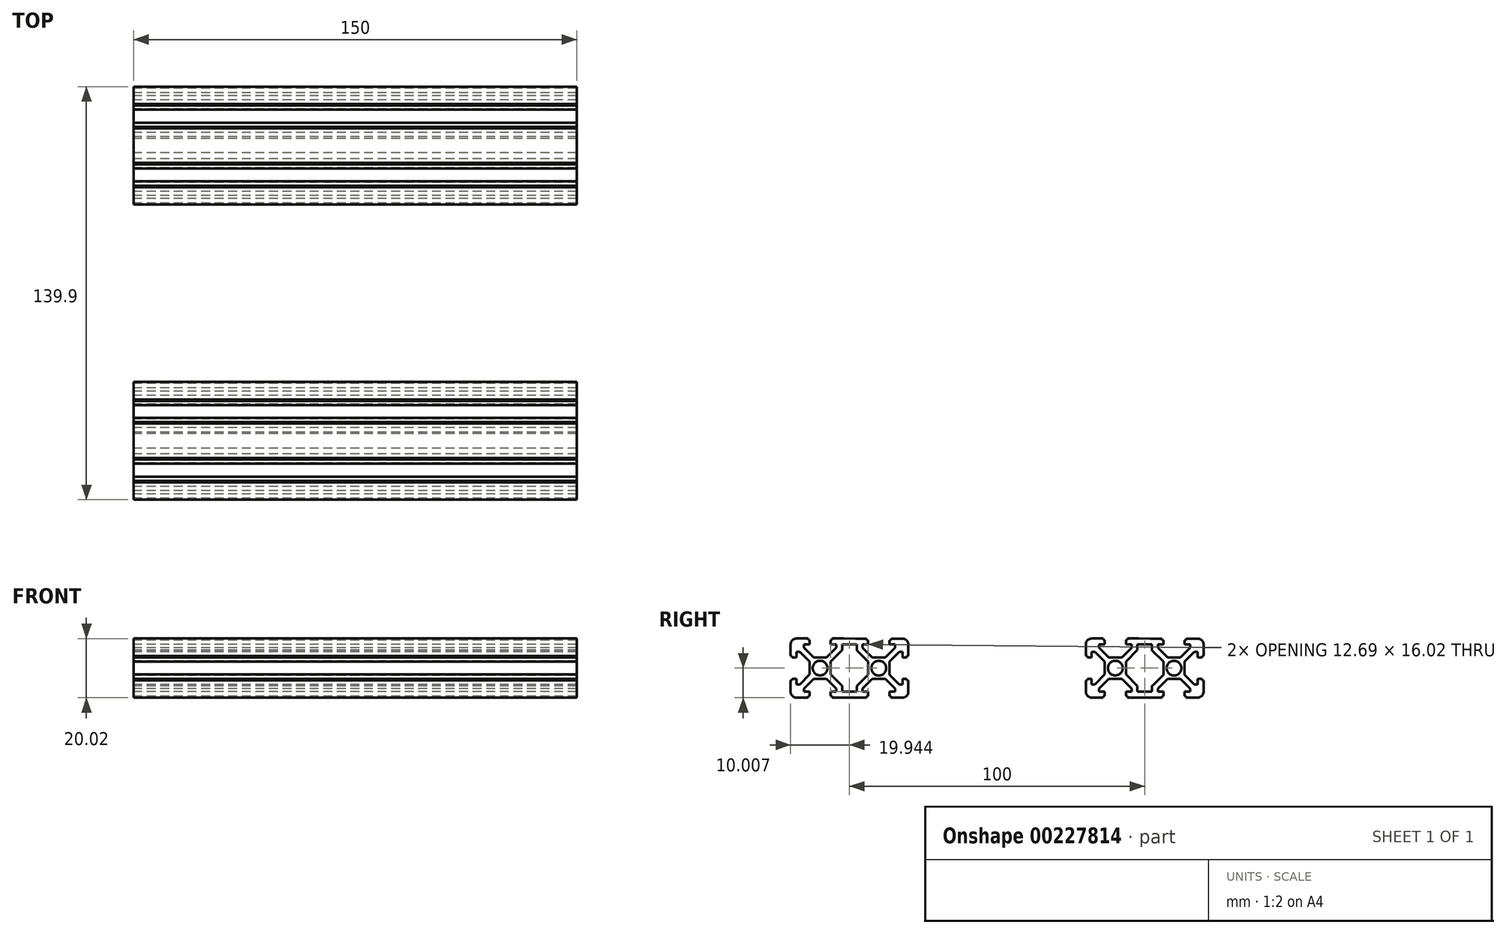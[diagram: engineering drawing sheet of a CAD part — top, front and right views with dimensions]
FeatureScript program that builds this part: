
annotation { "Feature Type Name" : "Feature", "Feature Type Description" : "" }
export const myFeature = defineFeature(function(context is Context, id is Id, definition is map)
    precondition{}
    {
        {
            var Q0;
            Q0=qCreatedBy(makeId("Right.planeOp"),FACE);
            var sketch = newSketch(context, id + "F0", { "sketchPlane" : qUnion([Q0])});
            skLineSegment(sketch, "E0", {"start": v(7.66, 9.4) * mm, "end": v(3.75, 9.4) * mm});
            skLineSegment(sketch, "E1", {"start": v(-8.35, -10.6) * mm, "end": v(-4.45, -10.6) * mm});
            skLineSegment(sketch, "E2", {"start": v(9.65, -8.6) * mm, "end": v(9.65, -4.7) * mm});
            skLineSegment(sketch, "E3", {"start": v(9.65, 9.4) * mm, "end": v(9.65, 9.37) * mm});
            skCircle(sketch, "E4", {"center": v(-0.35, -0.6) * mm, "radius": 2.5 * mm});
            skLineSegment(sketch, "E5", {"start": v(-3.95, -0.6) * mm, "end": v(-3.95, 1.6) * mm});
            skLineSegment(sketch, "E6", {"start": v(-0.35, 3) * mm, "end": v(-2.54, 3) * mm});
            skLineSegment(sketch, "E7", {"start": v(3.25, -0.6) * mm, "end": v(3.25, 1.6) * mm});
            skLineSegment(sketch, "E8", {"start": v(3.25, 8.9) * mm, "end": v(3.25, 7.4) * mm});
            skLineSegment(sketch, "E9", {"start": v(-0.35, -4.2) * mm, "end": v(1.83, -4.2) * mm});
            skLineSegment(sketch, "E10", {"start": v(9.15, -4.2) * mm, "end": v(7.65, -4.2) * mm});
            skLineSegment(sketch, "E11", {"start": v(-3.95, -0.6) * mm, "end": v(-3.95, -2.78) * mm});
            skLineSegment(sketch, "E12.0", {"start": v(-7.27, 4.9) * mm, "end": v(-3.95, 1.6) * mm});
            skLineSegment(sketch, "E13.0", {"start": v(9.67, 9.39) * mm, "end": v(9.65, 9.37) * mm});
            skLineSegment(sketch, "E14.0", {"start": v(5.15, 6.32) * mm, "end": v(1.83, 3) * mm});
            skPoint(sketch, "E15.startSnap0", {"position": v(-0.35, 9.4) * mm});
            skLineSegment(sketch, "E16", {"start": v(5.15, 7.4) * mm, "end": v(5.15, 6.32) * mm});
            skLineSegment(sketch, "E17", {"start": v(7.65, -6.1) * mm, "end": v(6.56, -6.1) * mm});
            skLineSegment(sketch, "E18", {"start": v(7.65, 4.9) * mm, "end": v(6.56, 4.9) * mm});
            skLineSegment(sketch, "E19", {"start": v(-5.85, 7.4) * mm, "end": v(-5.85, 6.32) * mm});
            skLineSegment(sketch, "E20.trimOffspring", {"start": v(-4.45, 9.4) * mm, "end": v(-8.35, 9.4) * mm});
            skLineSegment(sketch, "E21.trimOffspring", {"start": v(-3.95, 7.4) * mm, "end": v(-5.85, 7.4) * mm});
            skLineSegment(sketch, "E22.trimOffspring", {"start": v(3.25, 7.4) * mm, "end": v(3.25, 8.9) * mm});
            skLineSegment(sketch, "E23.trimOffspring", {"start": v(-3.95, 7.4) * mm, "end": v(-3.95, 8.9) * mm});
            skPoint(sketch, "E15.start.orphan", {"position": v(-0.35, 12.95) * mm});
            skLineSegment(sketch, "E24.trimOffspring", {"start": v(-2.54, 3) * mm, "end": v(1.83, 3) * mm});
            skLineSegment(sketch, "E25.trimOffspring", {"start": v(3.75, -10.6) * mm, "end": v(7.65, -10.6) * mm});
            skLineSegment(sketch, "E26.trimOffspring", {"start": v(3.25, -8.6) * mm, "end": v(5.15, -8.6) * mm});
            skLineSegment(sketch, "E27.trimOffspring", {"start": v(-3.95, -8.6) * mm, "end": v(-3.95, -10.1) * mm});
            skLineSegment(sketch, "E28.trimOffspring", {"start": v(3.25, -8.6) * mm, "end": v(3.25, -10.1) * mm});
            skLineSegment(sketch, "E29.trimOffspring", {"start": v(7.65, 3) * mm, "end": v(9.15, 3) * mm});
            skLineSegment(sketch, "E30.trimOffspring", {"start": v(1.83, -4.2) * mm, "end": v(-2.54, -4.2) * mm});
            skLineSegment(sketch, "E31.trimOffspring", {"start": v(7.65, -4.2) * mm, "end": v(9.15, -4.2) * mm});
            skLineSegment(sketch, "E32.trimOffspring", {"start": v(6.56, 4.9) * mm, "end": v(3.25, 1.6) * mm});
            skLineSegment(sketch, "E33.trimOffspring", {"start": v(5.15, 7.4) * mm, "end": v(3.25, 7.4) * mm});
            skLineSegment(sketch, "E34.trimOffspring", {"start": v(7.65, 4.9) * mm, "end": v(7.65, 3) * mm});
            skLineSegment(sketch, "E35.trimOffspring", {"start": v(9.65, 4.9) * mm, "end": v(9.65, 3.5) * mm});
            skLineSegment(sketch, "E36", {"start": v(9.66, 7.4) * mm, "end": v(9.65, 4.9) * mm});
            skLineSegment(sketch, "E37.trimOffspring", {"start": v(3.25, 1.6) * mm, "end": v(3.25, -2.78) * mm});
            skLineSegment(sketch, "E38.trimOffspring", {"start": v(3.25, -2.78) * mm, "end": v(6.56, -6.1) * mm});
            skLineSegment(sketch, "E39.trimOffspring", {"start": v(-2.54, -4.2) * mm, "end": v(-5.85, -7.5) * mm});
            skLineSegment(sketch, "E40.trimOffspring", {"start": v(1.83, -4.2) * mm, "end": v(5.15, -7.5) * mm});
            skLineSegment(sketch, "E41.trimOffspring", {"start": v(-3.95, -2.78) * mm, "end": v(-7.27, -6.1) * mm});
            skLineSegment(sketch, "E42.trimOffspring", {"start": v(-0.26, -0.6) * mm, "end": v(-0.24, -0.61) * mm});
            skLineSegment(sketch, "E43.trimOffspring", {"start": v(-5.85, 6.32) * mm, "end": v(-2.54, 3) * mm});
            skLineSegment(sketch, "E44.trimOffspring", {"start": v(-5.85, -7.5) * mm, "end": v(-5.85, -8.6) * mm});
            skLineSegment(sketch, "E45.trimOffspring", {"start": v(-5.85, -8.6) * mm, "end": v(-3.95, -8.6) * mm});
            skLineSegment(sketch, "E46.trimOffspring", {"start": v(5.15, -7.5) * mm, "end": v(5.15, -8.6) * mm});
            skLineSegment(sketch, "E47.trimOffspring", {"start": v(7.65, -6.1) * mm, "end": v(7.65, -4.2) * mm});
            skPoint(sketch, "E48.visualSharp", {"position": v(-10.35, 9.4) * mm});
            skPoint(sketch, "E49.newPointA", {"position": v(9.65, 9.4) * mm});
            skArc(sketch, "E49.filletArc", {"start": v(9.66, 7.4) * mm, "mid": v(9.07, 8.82) * mm, "end": v(7.66, 9.4) * mm});
            skPoint(sketch, "E50.visualSharp", {"position": v(9.65, -10.6) * mm});
            skArc(sketch, "E50.filletArc", {"start": v(7.65, -10.6) * mm, "mid": v(9.06, -10) * mm, "end": v(9.65, -8.6) * mm});
            skPoint(sketch, "E51.visualSharp", {"position": v(-10.35, -10.6) * mm});
            skLineSegment(sketch, "E52", {"start": v(-3.95, -10.1) * mm, "end": v(-4.45, -10.1) * mm});
            skLineSegment(sketch, "E53", {"start": v(-4.45, -10.1) * mm, "end": v(-4.45, -10.6) * mm});
            skLineSegment(sketch, "E54", {"start": v(3.75, -10.6) * mm, "end": v(3.75, -10.1) * mm});
            skLineSegment(sketch, "E55", {"start": v(3.75, -10.1) * mm, "end": v(3.25, -10.1) * mm});
            skLineSegment(sketch, "E56", {"start": v(9.15, -4.2) * mm, "end": v(9.15, -4.7) * mm});
            skLineSegment(sketch, "E57", {"start": v(9.15, -4.7) * mm, "end": v(9.65, -4.7) * mm});
            skLineSegment(sketch, "E58", {"start": v(9.15, 3) * mm, "end": v(9.15, 3.5) * mm});
            skLineSegment(sketch, "E59", {"start": v(9.15, 3.5) * mm, "end": v(9.65, 3.5) * mm});
            skPoint(sketch, "E60.orphan", {"position": v(-10.35, -4.2) * mm});
            skPoint(sketch, "E61.start.orphan", {"position": v(9.65, 3) * mm});
            skPoint(sketch, "E62.start.orphan", {"position": v(3.25, -10.6) * mm});
            skPoint(sketch, "E63.orphan", {"position": v(-3.95, -10.6) * mm});
            skLineSegment(sketch, "E64", {"start": v(-3.95, 8.9) * mm, "end": v(-4.45, 8.9) * mm});
            skLineSegment(sketch, "E65", {"start": v(-4.45, 8.9) * mm, "end": v(-4.45, 9.4) * mm});
            skLineSegment(sketch, "E66", {"start": v(3.25, 8.9) * mm, "end": v(3.75, 8.9) * mm});
            skLineSegment(sketch, "E67", {"start": v(3.75, 8.9) * mm, "end": v(3.75, 9.4) * mm});
            skPoint(sketch, "E68.start.orphan", {"position": v(3.25, 9.4) * mm});
            skPoint(sketch, "E69.start.orphan", {"position": v(-3.95, 9.4) * mm});
            skLineSegment(sketch, "E70", {"start": v(-12.23, 9.43) * mm, "end": v(-16.14, 9.43) * mm});
            skLineSegment(sketch, "E71", {"start": v(-30.24, 7.43) * mm, "end": v(-30.24, 3.53) * mm});
            skLineSegment(sketch, "E72", {"start": v(-28.24, -10.57) * mm, "end": v(-24.34, -10.57) * mm});
            skLineSegment(sketch, "E73", {"start": v(-10.24, -4.7) * mm, "end": v(-10.24, -4.67) * mm});
            skLineSegment(sketch, "E74", {"start": v(-10.24, 9.43) * mm, "end": v(-10.24, 9.4) * mm});
            skCircle(sketch, "E75", {"center": v(-20.24, -0.57) * mm, "radius": 2.5 * mm});
            skLineSegment(sketch, "E76", {"start": v(-23.84, 4.45) * mm, "end": v(-23.84, 4.5) * mm});
            skLineSegment(sketch, "E77", {"start": v(-29.74, 3.03) * mm, "end": v(-28.24, 3.03) * mm});
            skLineSegment(sketch, "E78", {"start": v(-16.64, 4.45) * mm, "end": v(-16.64, 4.5) * mm});
            skLineSegment(sketch, "E79", {"start": v(-16.64, 8.93) * mm, "end": v(-16.64, 7.43) * mm});
            skLineSegment(sketch, "E80", {"start": v(-22.42, -4.17) * mm, "end": v(-18.05, -4.17) * mm});
            skLineSegment(sketch, "E81", {"start": v(-23.84, 4.5) * mm, "end": v(-23.84, 4.45) * mm});
            skLineSegment(sketch, "E82.0", {"start": v(-27.15, 4.93) * mm, "end": v(-23.84, 1.62) * mm});
            skLineSegment(sketch, "E83.0", {"start": v(-14.74, 6.35) * mm, "end": v(-18.05, 3.03) * mm});
            skPoint(sketch, "E84.startSnap0", {"position": v(-20.24, 9.43) * mm});
            skLineSegment(sketch, "E85", {"start": v(-14.74, 7.43) * mm, "end": v(-14.74, 6.35) * mm});
            skLineSegment(sketch, "E86", {"start": v(-25.74, 7.43) * mm, "end": v(-25.74, 6.35) * mm});
            skLineSegment(sketch, "E87.trimOffspring", {"start": v(-24.34, 9.43) * mm, "end": v(-28.24, 9.43) * mm});
            skLineSegment(sketch, "E88.trimOffspring", {"start": v(-23.84, 7.43) * mm, "end": v(-25.74, 7.43) * mm});
            skLineSegment(sketch, "E89.trimOffspring", {"start": v(-16.64, 7.43) * mm, "end": v(-16.64, 8.93) * mm});
            skLineSegment(sketch, "E90.trimOffspring", {"start": v(-23.84, 7.43) * mm, "end": v(-23.84, 8.93) * mm});
            skPoint(sketch, "E84.start.orphan", {"position": v(-20.24, 12.98) * mm});
            skLineSegment(sketch, "E91.trimOffspring", {"start": v(-30.24, -4.67) * mm, "end": v(-30.24, -8.57) * mm});
            skLineSegment(sketch, "E92.trimOffspring", {"start": v(-28.24, -4.17) * mm, "end": v(-28.24, -6.07) * mm});
            skLineSegment(sketch, "E93.trimOffspring", {"start": v(-22.42, 3.03) * mm, "end": v(-18.05, 3.03) * mm});
            skLineSegment(sketch, "E94.trimOffspring", {"start": v(-28.24, 3.03) * mm, "end": v(-29.74, 3.03) * mm});
            skLineSegment(sketch, "E95.trimOffspring", {"start": v(-28.24, -4.17) * mm, "end": v(-29.74, -4.17) * mm});
            skLineSegment(sketch, "E96.trimOffspring", {"start": v(-16.14, -10.57) * mm, "end": v(-12.24, -10.57) * mm});
            skLineSegment(sketch, "E97.trimOffspring", {"start": v(-16.64, -8.57) * mm, "end": v(-14.74, -8.57) * mm});
            skLineSegment(sketch, "E98.trimOffspring", {"start": v(-23.84, -8.57) * mm, "end": v(-23.84, -10.07) * mm});
            skLineSegment(sketch, "E99.trimOffspring", {"start": v(-16.64, -8.57) * mm, "end": v(-16.64, -10.07) * mm});
            skLineSegment(sketch, "E100.trimOffspring", {"start": v(-18.05, -4.17) * mm, "end": v(-22.42, -4.17) * mm});
            skLineSegment(sketch, "E101.trimOffspring", {"start": v(-13.32, 4.93) * mm, "end": v(-16.64, 1.62) * mm});
            skLineSegment(sketch, "E102.trimOffspring", {"start": v(-14.74, 7.43) * mm, "end": v(-16.64, 7.43) * mm});
            skLineSegment(sketch, "E103.trimOffspring", {"start": v(-16.64, 1.62) * mm, "end": v(-16.64, -2.75) * mm});
            skLineSegment(sketch, "E104.trimOffspring", {"start": v(-16.64, -2.75) * mm, "end": v(-13.32, -6.07) * mm});
            skLineSegment(sketch, "E105.trimOffspring", {"start": v(-22.42, -4.17) * mm, "end": v(-25.74, -7.48) * mm});
            skLineSegment(sketch, "E106.trimOffspring", {"start": v(-18.05, -4.17) * mm, "end": v(-14.74, -7.48) * mm});
            skLineSegment(sketch, "E107.trimOffspring", {"start": v(-23.84, -2.75) * mm, "end": v(-27.15, -6.07) * mm});
            skLineSegment(sketch, "E108.trimOffspring", {"start": v(-20.24, -0.57) * mm, "end": v(-20.22, -0.59) * mm});
            skLineSegment(sketch, "E109.trimOffspring", {"start": v(-28.24, 4.93) * mm, "end": v(-28.24, 3.03) * mm});
            skLineSegment(sketch, "E110.trimOffspring", {"start": v(-25.74, 6.35) * mm, "end": v(-22.42, 3.03) * mm});
            skLineSegment(sketch, "E111.trimOffspring", {"start": v(-27.15, 4.93) * mm, "end": v(-28.24, 4.93) * mm});
            skLineSegment(sketch, "E112.trimOffspring", {"start": v(-27.15, -6.07) * mm, "end": v(-28.24, -6.07) * mm});
            skLineSegment(sketch, "E113.trimOffspring", {"start": v(-25.74, -7.48) * mm, "end": v(-25.74, -8.57) * mm});
            skLineSegment(sketch, "E114.trimOffspring", {"start": v(-29, -9.37) * mm, "end": v(-30.2, -10.57) * mm});
            skLineSegment(sketch, "E115.trimOffspring", {"start": v(-25.74, -8.57) * mm, "end": v(-23.84, -8.57) * mm});
            skLineSegment(sketch, "E116.trimOffspring", {"start": v(-14.74, -7.48) * mm, "end": v(-14.74, -8.57) * mm});
            skPoint(sketch, "E117.visualSharp", {"position": v(-30.24, 9.43) * mm});
            skArc(sketch, "E117.filletArc", {"start": v(-28.24, 9.43) * mm, "mid": v(-29.65, 8.85) * mm, "end": v(-30.24, 7.43) * mm});
            skPoint(sketch, "E118.newPointA", {"position": v(-10.24, 9.43) * mm});
            skPoint(sketch, "E119.visualSharp", {"position": v(-10.24, -10.57) * mm});
            skPoint(sketch, "E120.visualSharp", {"position": v(-30.24, -10.57) * mm});
            skArc(sketch, "E120.filletArc", {"start": v(-30.24, -8.57) * mm, "mid": v(-29.65, -9.98) * mm, "end": v(-28.24, -10.57) * mm});
            skLineSegment(sketch, "E121", {"start": v(-29.74, 3.03) * mm, "end": v(-29.74, 3.53) * mm});
            skLineSegment(sketch, "E122", {"start": v(-29.74, 3.53) * mm, "end": v(-30.24, 3.53) * mm});
            skLineSegment(sketch, "E123", {"start": v(-29.74, -4.17) * mm, "end": v(-29.74, -4.67) * mm});
            skLineSegment(sketch, "E124", {"start": v(-29.74, -4.67) * mm, "end": v(-30.24, -4.67) * mm});
            skLineSegment(sketch, "E125", {"start": v(-23.84, -10.07) * mm, "end": v(-24.34, -10.07) * mm});
            skLineSegment(sketch, "E126", {"start": v(-24.34, -10.07) * mm, "end": v(-24.34, -10.57) * mm});
            skLineSegment(sketch, "E127", {"start": v(-16.14, -10.57) * mm, "end": v(-16.14, -10.07) * mm});
            skLineSegment(sketch, "E128", {"start": v(-16.14, -10.07) * mm, "end": v(-16.64, -10.07) * mm});
            skPoint(sketch, "E129.orphan", {"position": v(-30.24, -4.17) * mm});
            skPoint(sketch, "E130.start.orphan", {"position": v(-10.24, 3.03) * mm});
            skPoint(sketch, "E131.start.orphan", {"position": v(-16.64, -10.57) * mm});
            skPoint(sketch, "E132.orphan", {"position": v(-23.84, -10.57) * mm});
            skLineSegment(sketch, "E133", {"start": v(-23.84, 8.93) * mm, "end": v(-24.34, 8.93) * mm});
            skLineSegment(sketch, "E134", {"start": v(-24.34, 8.93) * mm, "end": v(-24.34, 9.43) * mm});
            skLineSegment(sketch, "E135", {"start": v(-16.64, 8.93) * mm, "end": v(-16.14, 8.93) * mm});
            skLineSegment(sketch, "E136", {"start": v(-16.14, 8.93) * mm, "end": v(-16.14, 9.43) * mm});
            skPoint(sketch, "E137.start.orphan", {"position": v(-16.64, 9.43) * mm});
            skPoint(sketch, "E138.start.orphan", {"position": v(-23.84, 9.43) * mm});
            skPoint(sketch, "E139.end.orphan", {"position": v(-10.24, 3.53) * mm});
            skLineSegment(sketch, "E140", {"start": v(-12.23, 9.43) * mm, "end": v(-8.35, 9.4) * mm});
            skArc(sketch, "E141.trimOffspring", {"start": v(-12.2, 9.43) * mm, "mid": v(-12.22, 9.43) * mm, "end": v(-12.23, 9.43) * mm});
            skLineSegment(sketch, "E142.trimOffspring", {"start": v(-23.84, 1.62) * mm, "end": v(-23.84, -2.75) * mm});
            skLineSegment(sketch, "E143", {"start": v(-12.24, -10.57) * mm, "end": v(-8.38, -10.6) * mm});
            skLineSegment(sketch, "E144", {"start": v(-8.38, -10.6) * mm, "end": v(-8.35, -10.6) * mm});
            skLineSegment(sketch, "E145.0", {"start": v(-12.74, 5.52) * mm, "end": v(-16.64, 1.62) * mm});
            skLineSegment(sketch, "E145.1", {"start": v(-12.74, 7.43) * mm, "end": v(-12.74, 5.52) * mm});
            skLineSegment(sketch, "E145.2", {"start": v(-12.74, 9.43) * mm, "end": v(-16.64, 9.43) * mm});
            skLineSegment(sketch, "E146.0", {"start": v(-7.85, 7.4) * mm, "end": v(-7.85, 6.32) * mm});
            skLineSegment(sketch, "E147", {"start": v(-7.27, 4.9) * mm, "end": v(-7.85, 5.5) * mm});
            skLineSegment(sketch, "E148", {"start": v(-7.85, 6.32) * mm, "end": v(-7.85, 5.5) * mm});
            skLineSegment(sketch, "E149", {"start": v(-12.74, 7.43) * mm, "end": v(-7.85, 7.4) * mm});
            skLineSegment(sketch, "E150.0", {"start": v(-12.74, -7.48) * mm, "end": v(-12.74, -8.57) * mm});
            skLineSegment(sketch, "E151.0", {"start": v(-7.85, -7.5) * mm, "end": v(-7.85, -8.6) * mm});
            skLineSegment(sketch, "E152", {"start": v(-13.32, -6.07) * mm, "end": v(-12.74, -6.65) * mm});
            skLineSegment(sketch, "E153", {"start": v(-7.27, -6.1) * mm, "end": v(-7.85, -6.7) * mm});
            skLineSegment(sketch, "E154", {"start": v(-12.74, -7.48) * mm, "end": v(-12.74, -6.65) * mm});
            skLineSegment(sketch, "E155", {"start": v(-7.85, -7.5) * mm, "end": v(-7.85, -6.7) * mm});
            skPoint(sketch, "E156.end.orphan", {"position": v(-10.35, -4.7) * mm});
            skLineSegment(sketch, "E157", {"start": v(-12.74, -8.57) * mm, "end": v(-7.85, -8.6) * mm});
            skSolve(sketch);
        }
        {
            var Q0;
            Q0=makeQuery(id+"F0.imprint","IMPRINT",FACE,{"disambiguationData":[TD([[makeQuery(id+"F0.imprint","IMPRINT",EDGE,{"derivedFrom":sQuery(id+"F0.wireOp",EDGE,"E0")}),1.0]])]});
            extrude(context, id + "F1", {"entities" : qUnion([Q0]), "depth" : 150 * mm});
        }
        {
            var Q0;
            Q0=makeQuery(id+"F1.opExtrude","SWEPT_BODY",BODY,{"disambiguationData":[OSD([sQuery(id+"F0.wireOp",EDGE,"E0"),sQuery(id+"F0.wireOp",EDGE,"E1"),sQuery(id+"F0.wireOp",EDGE,"E2"),sQuery(id+"F0.wireOp",EDGE,"E4"),sQuery(id+"F0.wireOp",EDGE,"E5"),sQuery(id+"F0.wireOp",EDGE,"E11"),sQuery(id+"F0.wireOp",EDGE,"E12.0"),sQuery(id+"F0.wireOp",EDGE,"E14.0"),sQuery(id+"F0.wireOp",EDGE,"E16"),sQuery(id+"F0.wireOp",EDGE,"E17"),sQuery(id+"F0.wireOp",EDGE,"E18"),sQuery(id+"F0.wireOp",EDGE,"E19"),sQuery(id+"F0.wireOp",EDGE,"E20.trimOffspring"),sQuery(id+"F0.wireOp",EDGE,"E21.trimOffspring"),sQuery(id+"F0.wireOp",EDGE,"E22.trimOffspring"),sQuery(id+"F0.wireOp",EDGE,"E23.trimOffspring"),sQuery(id+"F0.wireOp",EDGE,"E24.trimOffspring"),sQuery(id+"F0.wireOp",EDGE,"E25.trimOffspring"),sQuery(id+"F0.wireOp",EDGE,"E26.trimOffspring"),sQuery(id+"F0.wireOp",EDGE,"E27.trimOffspring"),sQuery(id+"F0.wireOp",EDGE,"E28.trimOffspring"),sQuery(id+"F0.wireOp",EDGE,"E29.trimOffspring"),sQuery(id+"F0.wireOp",EDGE,"E30.trimOffspring"),sQuery(id+"F0.wireOp",EDGE,"E31.trimOffspring"),sQuery(id+"F0.wireOp",EDGE,"E32.trimOffspring"),sQuery(id+"F0.wireOp",EDGE,"E33.trimOffspring"),sQuery(id+"F0.wireOp",EDGE,"E34.trimOffspring"),sQuery(id+"F0.wireOp",EDGE,"E35.trimOffspring"),sQuery(id+"F0.wireOp",EDGE,"E36"),sQuery(id+"F0.wireOp",EDGE,"E37.trimOffspring"),sQuery(id+"F0.wireOp",EDGE,"E38.trimOffspring"),sQuery(id+"F0.wireOp",EDGE,"E39.trimOffspring"),sQuery(id+"F0.wireOp",EDGE,"E40.trimOffspring"),sQuery(id+"F0.wireOp",EDGE,"E41.trimOffspring"),sQuery(id+"F0.wireOp",EDGE,"E43.trimOffspring"),sQuery(id+"F0.wireOp",EDGE,"E44.trimOffspring"),sQuery(id+"F0.wireOp",EDGE,"E45.trimOffspring"),sQuery(id+"F0.wireOp",EDGE,"E46.trimOffspring"),sQuery(id+"F0.wireOp",EDGE,"E47.trimOffspring"),sQuery(id+"F0.wireOp",EDGE,"E49.filletArc"),sQuery(id+"F0.wireOp",EDGE,"E50.filletArc"),sQuery(id+"F0.wireOp",EDGE,"E52"),sQuery(id+"F0.wireOp",EDGE,"E53"),sQuery(id+"F0.wireOp",EDGE,"E54"),sQuery(id+"F0.wireOp",EDGE,"E55"),sQuery(id+"F0.wireOp",EDGE,"E56"),sQuery(id+"F0.wireOp",EDGE,"E57"),sQuery(id+"F0.wireOp",EDGE,"E58"),sQuery(id+"F0.wireOp",EDGE,"E59"),sQuery(id+"F0.wireOp",EDGE,"E64"),sQuery(id+"F0.wireOp",EDGE,"E65"),sQuery(id+"F0.wireOp",EDGE,"E66"),sQuery(id+"F0.wireOp",EDGE,"E67"),sQuery(id+"F0.wireOp",EDGE,"E70"),sQuery(id+"F0.wireOp",EDGE,"E71"),sQuery(id+"F0.wireOp",EDGE,"E72"),sQuery(id+"F0.wireOp",EDGE,"E75"),sQuery(id+"F0.wireOp",EDGE,"E82.0"),sQuery(id+"F0.wireOp",EDGE,"E83.0"),sQuery(id+"F0.wireOp",EDGE,"E85"),sQuery(id+"F0.wireOp",EDGE,"E86"),sQuery(id+"F0.wireOp",EDGE,"E87.trimOffspring"),sQuery(id+"F0.wireOp",EDGE,"E88.trimOffspring"),sQuery(id+"F0.wireOp",EDGE,"E89.trimOffspring"),sQuery(id+"F0.wireOp",EDGE,"E90.trimOffspring"),sQuery(id+"F0.wireOp",EDGE,"E91.trimOffspring"),sQuery(id+"F0.wireOp",EDGE,"E92.trimOffspring"),sQuery(id+"F0.wireOp",EDGE,"E93.trimOffspring"),sQuery(id+"F0.wireOp",EDGE,"E94.trimOffspring"),sQuery(id+"F0.wireOp",EDGE,"E95.trimOffspring"),sQuery(id+"F0.wireOp",EDGE,"E96.trimOffspring"),sQuery(id+"F0.wireOp",EDGE,"E97.trimOffspring"),sQuery(id+"F0.wireOp",EDGE,"E98.trimOffspring"),sQuery(id+"F0.wireOp",EDGE,"E99.trimOffspring"),sQuery(id+"F0.wireOp",EDGE,"E100.trimOffspring"),sQuery(id+"F0.wireOp",EDGE,"E102.trimOffspring"),sQuery(id+"F0.wireOp",EDGE,"E103.trimOffspring"),sQuery(id+"F0.wireOp",EDGE,"E104.trimOffspring"),sQuery(id+"F0.wireOp",EDGE,"E105.trimOffspring"),sQuery(id+"F0.wireOp",EDGE,"E106.trimOffspring"),sQuery(id+"F0.wireOp",EDGE,"E107.trimOffspring"),sQuery(id+"F0.wireOp",EDGE,"E109.trimOffspring"),sQuery(id+"F0.wireOp",EDGE,"E110.trimOffspring"),sQuery(id+"F0.wireOp",EDGE,"E111.trimOffspring"),sQuery(id+"F0.wireOp",EDGE,"E112.trimOffspring"),sQuery(id+"F0.wireOp",EDGE,"E113.trimOffspring"),sQuery(id+"F0.wireOp",EDGE,"E115.trimOffspring"),sQuery(id+"F0.wireOp",EDGE,"E116.trimOffspring"),sQuery(id+"F0.wireOp",EDGE,"E117.filletArc"),sQuery(id+"F0.wireOp",EDGE,"E120.filletArc"),sQuery(id+"F0.wireOp",EDGE,"E121"),sQuery(id+"F0.wireOp",EDGE,"E122"),sQuery(id+"F0.wireOp",EDGE,"E123"),sQuery(id+"F0.wireOp",EDGE,"E124"),sQuery(id+"F0.wireOp",EDGE,"E125"),sQuery(id+"F0.wireOp",EDGE,"E126"),sQuery(id+"F0.wireOp",EDGE,"E127"),sQuery(id+"F0.wireOp",EDGE,"E128"),sQuery(id+"F0.wireOp",EDGE,"E133"),sQuery(id+"F0.wireOp",EDGE,"E134"),sQuery(id+"F0.wireOp",EDGE,"E135"),sQuery(id+"F0.wireOp",EDGE,"E136"),sQuery(id+"F0.wireOp",EDGE,"E140"),sQuery(id+"F0.wireOp",EDGE,"E142.trimOffspring"),sQuery(id+"F0.wireOp",EDGE,"E143"),sQuery(id+"F0.wireOp",EDGE,"E144"),sQuery(id+"F0.wireOp",EDGE,"E145.0"),sQuery(id+"F0.wireOp",EDGE,"E145.1"),sQuery(id+"F0.wireOp",EDGE,"E145.2"),sQuery(id+"F0.wireOp",EDGE,"E146.0"),sQuery(id+"F0.wireOp",EDGE,"E147"),sQuery(id+"F0.wireOp",EDGE,"E148"),sQuery(id+"F0.wireOp",EDGE,"E149"),sQuery(id+"F0.wireOp",EDGE,"E150.0"),sQuery(id+"F0.wireOp",EDGE,"E151.0"),sQuery(id+"F0.wireOp",EDGE,"E152"),sQuery(id+"F0.wireOp",EDGE,"E153"),sQuery(id+"F0.wireOp",EDGE,"E154"),sQuery(id+"F0.wireOp",EDGE,"E155"),sQuery(id+"F0.wireOp",EDGE,"E157")])]});
            var Q1;
            Q1=makeQuery(id+"F1.opExtrude","CAP_EDGE",EDGE,{"disambiguationData":[OSD([sQuery(id+"F0.wireOp",EDGE,"E143"),sQuery(id+"F0.wireOp",EDGE,"E144")])],"isStart":false});
            transform(context, id + "F2", {"entities" : qUnion([Q0]), "transformType" : TransformType.TRANSLATION_3D, "dx" : 0 * mm, "dy" : 100 * mm, "dz" : 0 * mm, "makeCopy" : true});
        }
    });
